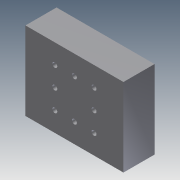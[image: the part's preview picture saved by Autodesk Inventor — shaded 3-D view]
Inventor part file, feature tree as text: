
AUTODESK INVENTOR PART (.ipt)
format: ipt  version: 2011 (Build 150239000, 239)  size: 149,504 bytes
history: native  units: in
note: dims shown in document units (in); Inventor stores cm internally (conversion verified against a paired STEP export)
features: extrude x7, sketch x7
ambient origin geometry x8: Origin, YZ Plane, XZ Plane, XY Plane, X Axis, Y Axis, Z Axis, Center Point
bodies: Solid1 (feature_tree)
feature tree (14):
  extrude  "Extrusion1"  Depth=1.1811in
  extrude  "Extrusion2"  Depth=0.315in
  extrude  "Extrusion3"  Depth=0.6299in
  extrude  "Extrusion4"  Depth=0.6299in
  extrude  "Extrusion5"  Depth=0.0787in TaperAngle=0.0deg
  extrude  "Extrusion6"  Depth=0.0394in TaperAngle=0.0deg
  extrude  "Extrusion7"  Depth=0.046in TaperAngle=0.0deg
  sketch  "Sketch1"  dims[d0=1.5748in d1=1.1811in]
  sketch  "Sketch2"  dims[d2=0.0787in d3=0.0in d4=0.315in]
  sketch  "Sketch3"  dims[d5=0.315in d6=0.6299in]
  sketch  "Sketch4"  dims[d7=0.6299in d8=0.6299in]
  sketch  "Sketch5"  dims[d9=0.0787in d10=0.0787in d11=0.0in]
  sketch  "Sketch6"  dims[d12=0.0394in d13=0.0in d14=0.0394in d15=0.0in]
  sketch  "Sketch7"  dims[d16=0.375in d17=0.0in d18=0.046in d19=0.0in d20=0.0394in d21=2.0in d22=0.0in]
